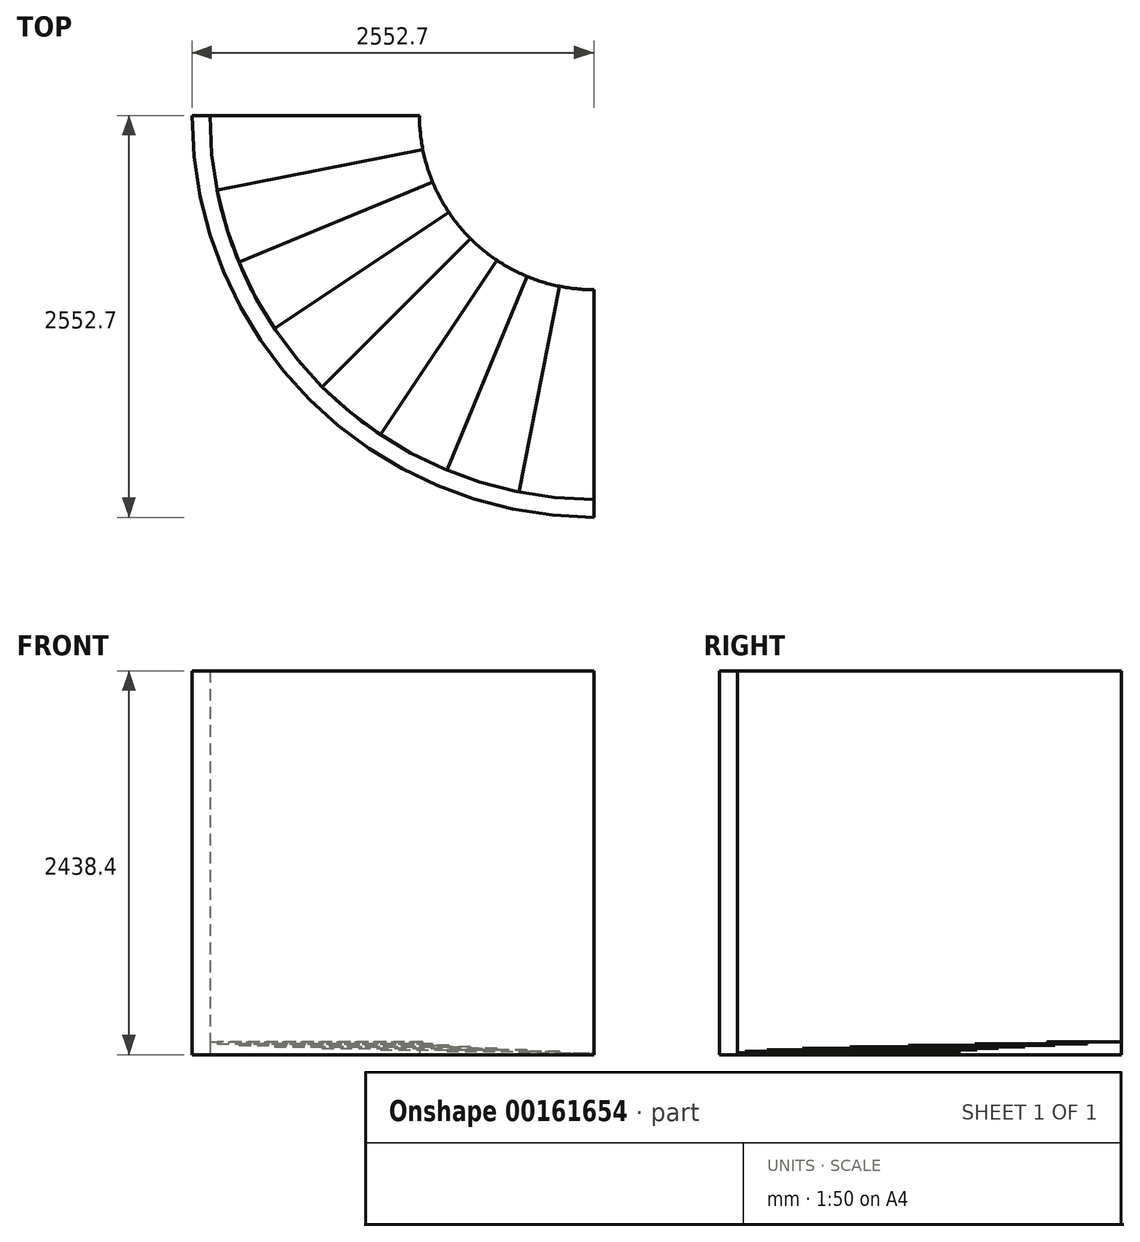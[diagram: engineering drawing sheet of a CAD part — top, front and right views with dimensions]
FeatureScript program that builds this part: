
annotation { "Feature Type Name" : "Feature", "Feature Type Description" : "" }
export const myFeature = defineFeature(function(context is Context, id is Id, definition is map)
    precondition{}
    {
        {
            assignVariable(context, id + "F0", {"name" : "StepHeight", "anyValue" : 10});
        }
        {
            var Q0;
            Q0=qCreatedBy(makeId("Top.planeOp"),FACE);
            var sketch = newSketch(context, id + "F1", { "sketchPlane" : qUnion([Q0])});
            skLineSegment(sketch, "E0", {"start": v(0, 0) * mm, "end": v(0, -1331.38) * mm, "construction": true});
            skLineSegment(sketch, "E1", {"start": v(0, -1331.38) * mm, "end": v(-979.53, -1331.38) * mm, "construction": true});
            skLineSegment(sketch, "E2", {"start": v(-979.53, -1331.38) * mm, "end": v(-3417.93, 1107.02) * mm, "construction": true});
            skLineSegment(sketch, "E3", {"start": v(-3417.93, 1107.02) * mm, "end": v(-3417.93, 2307.05) * mm, "construction": true});
            skLineSegment(sketch, "E4", {"start": v(-3417.93, 2307.05) * mm, "end": v(-2086.54, 2307.05) * mm, "construction": true});
            skLineSegment(sketch, "E5", {"start": v(-2086.54, 2307.05) * mm, "end": v(-2086.54, 1107.02) * mm, "construction": true});
            skLineSegment(sketch, "E6", {"start": v(-2086.54, 1107.02) * mm, "end": v(-979.53, 0) * mm, "construction": true});
            skLineSegment(sketch, "E7", {"start": v(-979.53, 0) * mm, "end": v(0, 0) * mm, "construction": true});
            skArc(sketch, "E8", {"start": v(-3417.93, 1107.02) * mm, "mid": v(-2703.74, -617.2) * mm, "end": v(-979.53, -1331.38) * mm, "construction": true});
            skArc(sketch, "E9", {"start": v(-2086.54, 1107.02) * mm, "mid": v(-1762.3, 324.24) * mm, "end": v(-979.53, 0) * mm, "construction": true});
            skSolve(sketch);
        }
        {
            var Q0;
            Q0=qCreatedBy(makeId("Top.planeOp"),FACE);
            var sketch = newSketch(context, id + "F2", { "sketchPlane" : qUnion([Q0])});
            skLineSegment(sketch, "E10", {"start": v(-979.53, 0) * mm, "end": v(-979.53, -1331.38) * mm});
            skLineSegment(sketch, "E11", {"start": v(-1455.24, -1284.53) * mm, "end": v(-1195.5, 21.27) * mm});
            skArc(sketch, "E12", {"start": v(-1195.5, 21.27) * mm, "mid": v(-1088.03, 5.33) * mm, "end": v(-979.53, 0) * mm});
            skArc(sketch, "E13", {"start": v(-1455.24, -1284.53) * mm, "mid": v(-1218.53, -1319.64) * mm, "end": v(-979.53, -1331.38) * mm});
            skLineSegment(sketch, "E14", {"start": v(-979.53, -1331.38) * mm, "end": v(-1455.24, -1284.53) * mm, "construction": true});
            skLineSegment(sketch, "E15", {"start": v(-1325.37, -631.63) * mm, "end": v(-979.53, -665.7) * mm, "construction": true});
            skSolve(sketch);
        }
        {
            var Q0;
            Q0=qCreatedBy(makeId("Top.planeOp"),FACE);
            var sketch = newSketch(context, id + "F3", { "sketchPlane" : qUnion([Q0])});
            skLineSegment(sketch, "E16", {"start": v(-1195.5, 21.27) * mm, "end": v(-1455.24, -1284.53) * mm});
            skLineSegment(sketch, "E17", {"start": v(-1912.66, -1145.77) * mm, "end": v(-1403.16, 84.27) * mm});
            skArc(sketch, "E18", {"start": v(-1403.16, 84.27) * mm, "mid": v(-1300.88, 47.67) * mm, "end": v(-1195.5, 21.27) * mm});
            skArc(sketch, "E19", {"start": v(-1912.66, -1145.77) * mm, "mid": v(-1687.36, -1226.39) * mm, "end": v(-1455.24, -1284.53) * mm});
            skLineSegment(sketch, "E20", {"start": v(-1455.24, -1284.53) * mm, "end": v(-1912.66, -1145.77) * mm, "construction": true});
            skSolve(sketch);
        }
        {
            var Q0;
            Q0=qCreatedBy(makeId("Top.planeOp"),FACE);
            var sketch = newSketch(context, id + "F4", { "sketchPlane" : qUnion([Q0])});
            skLineSegment(sketch, "E21", {"start": v(-1403.16, 84.27) * mm, "end": v(-1912.66, -1145.77) * mm});
            skLineSegment(sketch, "E22", {"start": v(-2334.23, -920.44) * mm, "end": v(-1594.55, 186.57) * mm});
            skArc(sketch, "E23", {"start": v(-1594.55, 186.57) * mm, "mid": v(-1501.37, 130.72) * mm, "end": v(-1403.16, 84.27) * mm});
            skArc(sketch, "E24", {"start": v(-2334.23, -920.44) * mm, "mid": v(-2128.98, -1043.46) * mm, "end": v(-1912.66, -1145.77) * mm});
            skLineSegment(sketch, "E25", {"start": v(-1912.66, -1145.77) * mm, "end": v(-2334.23, -920.44) * mm, "construction": true});
            skSolve(sketch);
        }
        {
            var Q0;
            Q0=qCreatedBy(makeId("Top.planeOp"),FACE);
            var sketch = newSketch(context, id + "F5", { "sketchPlane" : qUnion([Q0])});
            skLineSegment(sketch, "E26", {"start": v(-1594.55, 186.57) * mm, "end": v(-2334.23, -920.44) * mm});
            skLineSegment(sketch, "E27", {"start": v(-2703.74, -617.2) * mm, "end": v(-1762.3, 324.24) * mm});
            skArc(sketch, "E28", {"start": v(-1762.3, 324.24) * mm, "mid": v(-1681.81, 251.28) * mm, "end": v(-1594.55, 186.57) * mm});
            skArc(sketch, "E29", {"start": v(-2703.74, -617.2) * mm, "mid": v(-2526.43, -777.9) * mm, "end": v(-2334.23, -920.44) * mm});
            skLineSegment(sketch, "E30", {"start": v(-2334.23, -920.44) * mm, "end": v(-2703.74, -617.2) * mm, "construction": true});
            skSolve(sketch);
        }
        {
            var Q0;
            Q0=qCreatedBy(makeId("Top.planeOp"),FACE);
            var sketch = newSketch(context, id + "F6", { "sketchPlane" : qUnion([Q0])});
            skLineSegment(sketch, "E31", {"start": v(-1762.3, 324.24) * mm, "end": v(-2703.74, -617.2) * mm});
            skLineSegment(sketch, "E32", {"start": v(-3006.98, -247.69) * mm, "end": v(-1899.98, 492) * mm});
            skArc(sketch, "E33", {"start": v(-1899.98, 492) * mm, "mid": v(-1835.26, 404.73) * mm, "end": v(-1762.3, 324.24) * mm});
            skArc(sketch, "E34", {"start": v(-3006.98, -247.69) * mm, "mid": v(-2864.44, -439.89) * mm, "end": v(-2703.74, -617.2) * mm});
            skLineSegment(sketch, "E35", {"start": v(-2703.74, -617.2) * mm, "end": v(-3006.98, -247.69) * mm, "construction": true});
            skSolve(sketch);
        }
        {
            var Q0;
            Q0=qCreatedBy(makeId("Top.planeOp"),FACE);
            var sketch = newSketch(context, id + "F7", { "sketchPlane" : qUnion([Q0])});
            skLineSegment(sketch, "E36", {"start": v(-1899.98, 492) * mm, "end": v(-3006.98, -247.69) * mm});
            skLineSegment(sketch, "E37", {"start": v(-3232.31, 173.88) * mm, "end": v(-2002.28, 683.38) * mm});
            skArc(sketch, "E38", {"start": v(-2002.28, 683.38) * mm, "mid": v(-1955.83, 585.17) * mm, "end": v(-1899.98, 492) * mm});
            skArc(sketch, "E39", {"start": v(-3232.31, 173.88) * mm, "mid": v(-3130, -42.44) * mm, "end": v(-3006.98, -247.69) * mm});
            skLineSegment(sketch, "E40", {"start": v(-3006.98, -247.69) * mm, "end": v(-3232.31, 173.88) * mm, "construction": true});
            skSolve(sketch);
        }
        {
            var Q0;
            Q0=qCreatedBy(makeId("Top.planeOp"),FACE);
            var sketch = newSketch(context, id + "F8", { "sketchPlane" : qUnion([Q0])});
            skLineSegment(sketch, "E41", {"start": v(-2002.28, 683.38) * mm, "end": v(-3232.31, 173.88) * mm});
            skLineSegment(sketch, "E42", {"start": v(-3371.07, 631.3) * mm, "end": v(-2065.27, 891.05) * mm});
            skArc(sketch, "E43", {"start": v(-2065.27, 891.05) * mm, "mid": v(-2038.88, 785.67) * mm, "end": v(-2002.28, 683.38) * mm});
            skArc(sketch, "E44", {"start": v(-3371.07, 631.3) * mm, "mid": v(-3312.93, 399.19) * mm, "end": v(-3232.31, 173.88) * mm});
            skLineSegment(sketch, "E45", {"start": v(-3232.31, 173.88) * mm, "end": v(-3371.07, 631.3) * mm, "construction": true});
            skSolve(sketch);
        }
        {
            var Q0;
            Q0=qCreatedBy(makeId("Top.planeOp"),FACE);
            var sketch = newSketch(context, id + "F9", { "sketchPlane" : qUnion([Q0])});
            skLineSegment(sketch, "E46", {"start": v(-2065.27, 891.05) * mm, "end": v(-3371.07, 631.3) * mm});
            skLineSegment(sketch, "E47", {"start": v(-3417.93, 1107.02) * mm, "end": v(-2086.54, 1107.02) * mm});
            skArc(sketch, "E48", {"start": v(-2086.54, 1107.02) * mm, "mid": v(-2081.21, 998.51) * mm, "end": v(-2065.27, 891.05) * mm});
            skArc(sketch, "E49", {"start": v(-3417.93, 1107.02) * mm, "mid": v(-3406.19, 868.01) * mm, "end": v(-3371.07, 631.3) * mm});
            skLineSegment(sketch, "E50", {"start": v(-3371.07, 631.3) * mm, "end": v(-3417.93, 1107.02) * mm, "construction": true});
            skSolve(sketch);
        }
        {
            var Q0;
            Q0=qSketchRegion(id+"F2",true);
            extrude(context, id + "F10", {"entities" : qUnion([Q0]), "depth" : (getVariable(context, 'StepHeight')) * mm});
        }
        {
            var Q0;
            Q0=qSketchRegion(id+"F3",true);
            extrude(context, id + "F11", {"entities" : qUnion([Q0]), "operationType" : NewBodyOperationType.ADD, "depth" : (getVariable(context, 'StepHeight') * 2) * mm});
        }
        {
            var Q0;
            Q0=qSketchRegion(id+"F4",true);
            extrude(context, id + "F12", {"entities" : qUnion([Q0]), "operationType" : NewBodyOperationType.ADD, "depth" : (getVariable(context, 'StepHeight') * 3) * mm});
        }
        {
            var Q0;
            Q0=qSketchRegion(id+"F5",true);
            extrude(context, id + "F13", {"entities" : qUnion([Q0]), "operationType" : NewBodyOperationType.ADD, "depth" : (getVariable(context, 'StepHeight') * 4) * mm});
        }
        {
            var Q0;
            Q0=qSketchRegion(id+"F6",true);
            extrude(context, id + "F14", {"entities" : qUnion([Q0]), "operationType" : NewBodyOperationType.ADD, "depth" : (getVariable(context, 'StepHeight') * 5) * mm});
        }
        {
            var Q0;
            Q0=qSketchRegion(id+"F7",true);
            extrude(context, id + "F15", {"entities" : qUnion([Q0]), "operationType" : NewBodyOperationType.ADD, "depth" : (getVariable(context, 'StepHeight') * 6) * mm});
        }
        {
            var Q0;
            Q0=qSketchRegion(id+"F8",true);
            extrude(context, id + "F16", {"entities" : qUnion([Q0]), "operationType" : NewBodyOperationType.ADD, "depth" : (getVariable(context, 'StepHeight') * 7) * mm});
        }
        {
            var Q0;
            Q0=qSketchRegion(id+"F9",true);
            extrude(context, id + "F17", {"entities" : qUnion([Q0]), "operationType" : NewBodyOperationType.ADD, "depth" : (getVariable(context, 'StepHeight') * 8) * mm});
        }
        {
            var Q0;
            Q0=qCreatedBy(makeId("Top.planeOp"),FACE);
            var sketch = newSketch(context, id + "F18", { "sketchPlane" : qUnion([Q0])});
            skArc(sketch, "E51", {"start": v(-3417.93, 1107.02) * mm, "mid": v(-2703.74, -617.2) * mm, "end": v(-979.53, -1331.38) * mm});
            skArc(sketch, "E52", {"start": v(-3532.23, 1107.02) * mm, "mid": v(-2784.56, -698.01) * mm, "end": v(-979.53, -1445.68) * mm});
            skLineSegment(sketch, "E53", {"start": v(-3417.93, 1107.02) * mm, "end": v(-3532.23, 1107.02) * mm});
            skLineSegment(sketch, "E54", {"start": v(-979.53, -1445.68) * mm, "end": v(-979.53, -1331.38) * mm});
            skSolve(sketch);
        }
        {
            var Q0;
            Q0 = qSketchRegion(id + "F18", true);
            extrude(context, id + "F19", {"entities" : qUnion([Q0]), "depth" : 8 * 304.8 * mm});
        }
    });
